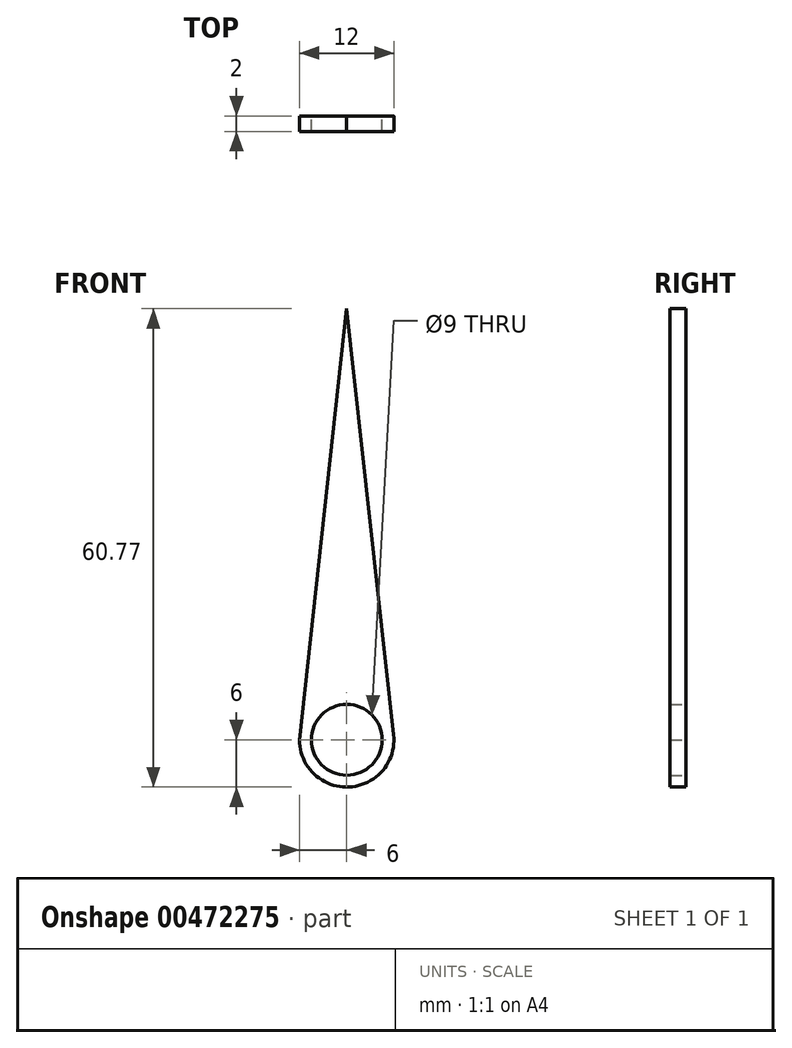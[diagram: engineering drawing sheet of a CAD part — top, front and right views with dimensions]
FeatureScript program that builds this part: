
annotation { "Feature Type Name" : "Feature", "Feature Type Description" : "" }
export const myFeature = defineFeature(function(context is Context, id is Id, definition is map)
    precondition{}
    {
        {
            var Q0;
            Q0=qCreatedBy(makeId("Front.planeOp"),FACE);
            var sketch = newSketch(context, id + "F0", { "sketchPlane" : qUnion([Q0])});
            skArc(sketch, "E0", {"start": v(-6, 0) * mm, "mid": v(0.33, -6) * mm, "end": v(5.96, 0.66) * mm});
            skCircle(sketch, "E1", {"center": v(0, 0) * mm, "radius": 4.5 * mm});
            skLineSegment(sketch, "E2", {"start": v(-6, 0) * mm, "end": v(0, 54.77) * mm});
            skLineSegment(sketch, "E3", {"start": v(0, 54.77) * mm, "end": v(5.96, 0.66) * mm});
            skPoint(sketch, "E4.orphan", {"position": v(6.04, 0) * mm});
            skSolve(sketch);
        }
        {
            var Q0;
            Q0 = qSketchRegion(id + "F0", true);
            extrude(context, id + "F1", {"entities" : qUnion([Q0]), "depth" : 2 * mm, "offsetDistance" : 25 * mm});
        }
    });
